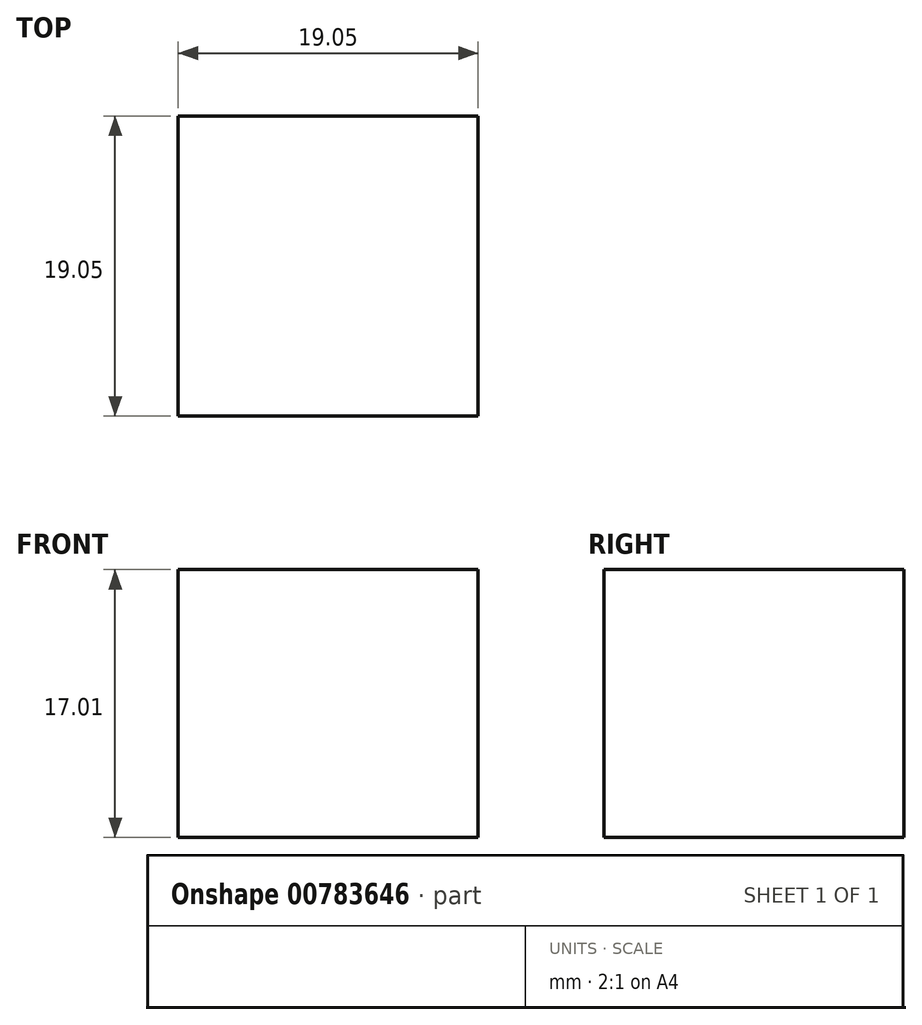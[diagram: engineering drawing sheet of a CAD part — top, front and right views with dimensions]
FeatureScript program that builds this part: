
annotation { "Feature Type Name" : "Feature", "Feature Type Description" : "" }
export const myFeature = defineFeature(function(context is Context, id is Id, definition is map)
    precondition{}
    {
        {
            var Q0;
            Q0=qCreatedBy(makeId("Front.planeOp"),FACE);
            var sketch = newSketch(context, id + "F0", { "sketchPlane" : qUnion([Q0])});
            skLineSegment(sketch, "E0.bottom", {"start": v(14.76, 6.42) * mm, "end": v(33.81, 6.42) * mm});
            skLineSegment(sketch, "E0.top", {"start": v(14.76, -10.59) * mm, "end": v(33.81, -10.59) * mm});
            skLineSegment(sketch, "E0.left", {"start": v(14.76, 6.42) * mm, "end": v(14.76, -10.59) * mm});
            skLineSegment(sketch, "E0.right", {"start": v(33.81, 6.42) * mm, "end": v(33.81, -10.59) * mm});
            skSolve(sketch);
        }
        {
            var Q0;
            Q0=makeQuery(id+"F0.imprint","IMPRINT",FACE,{"disambiguationData":[TD([[makeQuery(id+"F0.imprint","IMPRINT",EDGE,{"derivedFrom":sQuery(id+"F0.wireOp",EDGE,"E0.bottom")}),-1.0]])]});
            extrude(context, id + "F1", {"entities" : qUnion([Q0]), "depth" : 19.05 * mm, "offsetDistance" : 25.4 * mm});
        }
    });
